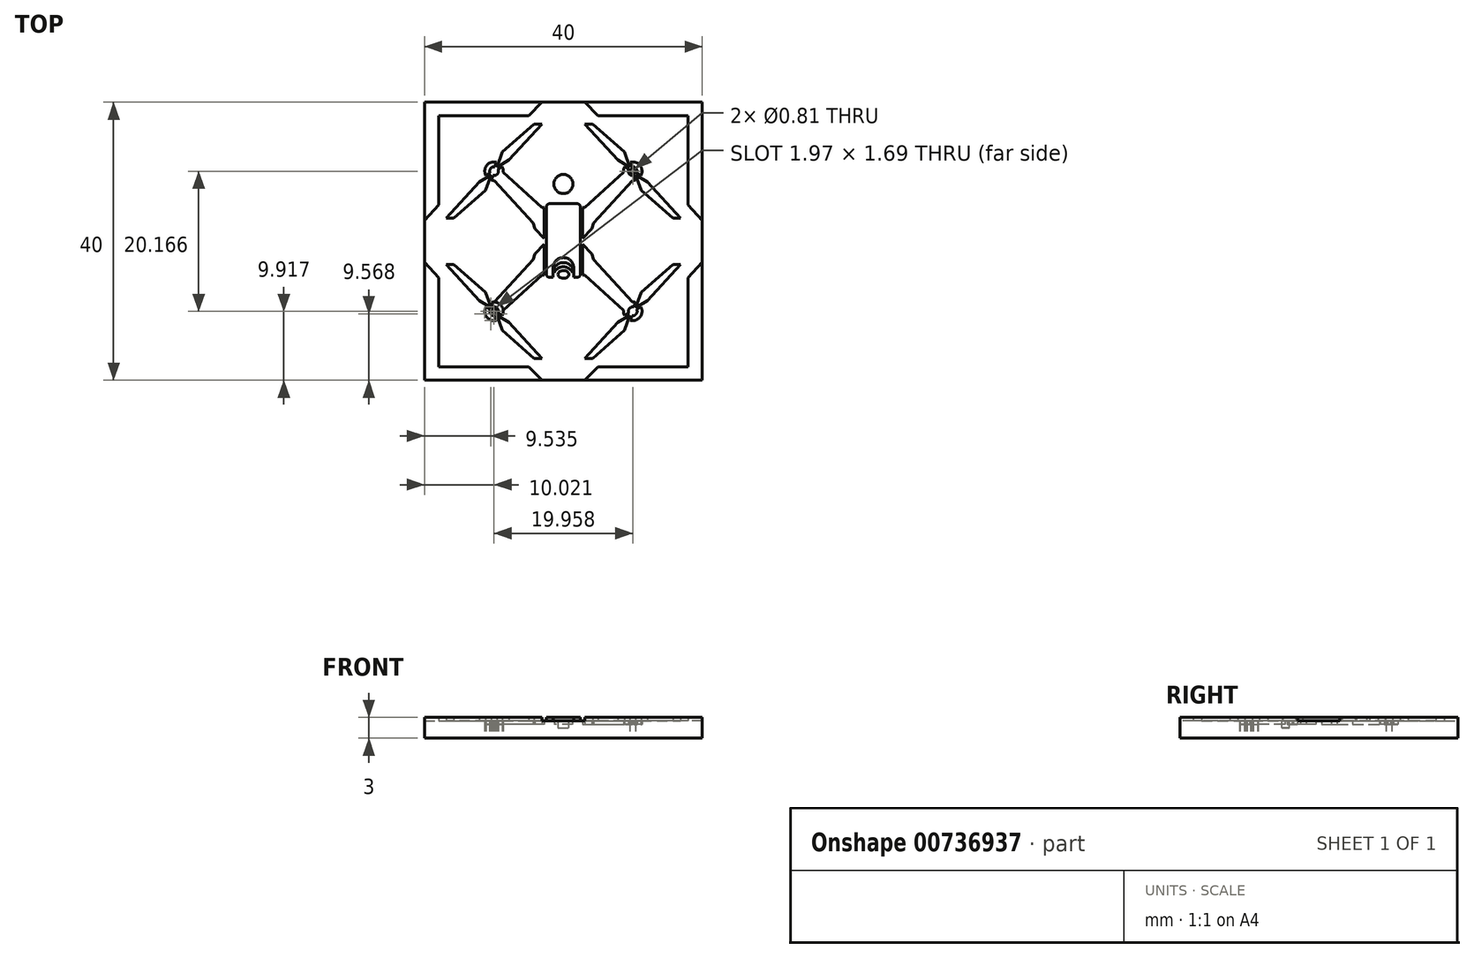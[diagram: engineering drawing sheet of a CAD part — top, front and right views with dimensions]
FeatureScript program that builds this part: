
annotation { "Feature Type Name" : "Feature", "Feature Type Description" : "" }
export const myFeature = defineFeature(function(context is Context, id is Id, definition is map)
    precondition{}
    {
        {
            var Q0;
            Q0=qCreatedBy(makeId("Top.planeOp"),FACE);
            var sketch = newSketch(context, id + "F0", { "sketchPlane" : qUnion([Q0])});
            skLineSegment(sketch, "E0.bottom", {"start": v(-20, 20) * mm, "end": v(20, 20) * mm});
            skLineSegment(sketch, "E0.top", {"start": v(-20, -20) * mm, "end": v(20, -20) * mm});
            skLineSegment(sketch, "E0.left", {"start": v(-20, 20) * mm, "end": v(-20, -20) * mm});
            skLineSegment(sketch, "E0.right", {"start": v(20, 20) * mm, "end": v(20, -20) * mm});
            skLineSegment(sketch, "E1", {"start": v(-20, 3.01) * mm, "end": v(-17.93, 5.25) * mm});
            skLineSegment(sketch, "E2", {"start": v(-17.93, 5.25) * mm, "end": v(-17.93, 18.07) * mm});
            skLineSegment(sketch, "E3", {"start": v(-17.93, 18.07) * mm, "end": v(-5, 18.07) * mm});
            skLineSegment(sketch, "E4", {"start": v(-5, 18.07) * mm, "end": v(-3.07, 20) * mm});
            skLineSegment(sketch, "E5", {"start": v(-16.86, 3.32) * mm, "end": v(-12.08, 8.54) * mm});
            skLineSegment(sketch, "E6", {"start": v(-12.08, 8.54) * mm, "end": v(-10.4, 9.57) * mm});
            skLineSegment(sketch, "E7", {"start": v(-10.4, 9.57) * mm, "end": v(-11.18, 7.35) * mm});
            skLineSegment(sketch, "E8", {"start": v(-11.18, 7.35) * mm, "end": v(-15.75, 3.32) * mm});
            skLineSegment(sketch, "E9", {"start": v(-15.75, 3.32) * mm, "end": v(-16.86, 3.32) * mm});
            skLineSegment(sketch, "E10", {"start": v(-9.53, 10.64) * mm, "end": v(-8.82, 12.83) * mm});
            skLineSegment(sketch, "E11", {"start": v(-8.82, 12.83) * mm, "end": v(-4.25, 16.86) * mm});
            skLineSegment(sketch, "E12", {"start": v(-4.25, 16.86) * mm, "end": v(-3.08, 16.86) * mm});
            skLineSegment(sketch, "E13", {"start": v(-3.08, 16.86) * mm, "end": v(-7.83, 11.68) * mm});
            skLineSegment(sketch, "E14", {"start": v(-7.83, 11.68) * mm, "end": v(-9.53, 10.64) * mm});
            skLineSegment(sketch, "E15", {"start": v(-2.75, 0.43) * mm, "end": v(-2.75, 4.84) * mm});
            skLineSegment(sketch, "E16", {"start": v(-2.75, 4.84) * mm, "end": v(-3.08, 4.84) * mm});
            skLineSegment(sketch, "E17", {"start": v(-3.08, 4.84) * mm, "end": v(-8.65, 9.93) * mm});
            skLineSegment(sketch, "E18", {"start": v(-2.75, 0.43) * mm, "end": v(-4.12, 1.8) * mm});
            skLineSegment(sketch, "E19", {"start": v(-4.12, 1.8) * mm, "end": v(-4.34, 2.63) * mm});
            skLineSegment(sketch, "E20", {"start": v(-4.34, 2.63) * mm, "end": v(-9.91, 8.74) * mm});
            skCircle(sketch, "E21", {"center": v(-9.98, 10.08) * mm, "radius": 0.4 * mm});
            skLineSegment(sketch, "E22", {"start": v(-11.15, 9.45) * mm, "end": v(-10.56, 9.84) * mm});
            skLineSegment(sketch, "E23", {"start": v(-9.86, 10.7) * mm, "end": v(-9.62, 11.37) * mm});
            skLineSegment(sketch, "E24", {"start": v(-10.14, 9.47) * mm, "end": v(-10.4, 8.82) * mm});
            skLineSegment(sketch, "E25", {"start": v(-9.4, 10.34) * mm, "end": v(-9.4, 10.34) * mm});
            skLineSegment(sketch, "E26", {"start": v(-9.4, 10.34) * mm, "end": v(-8.81, 10.73) * mm});
            skArc(sketch, "E27", {"start": v(-9.86, 10.7) * mm, "mid": v(-10.47, 10.48) * mm, "end": v(-10.56, 9.84) * mm});
            skLineSegment(sketch, "E28", {"start": v(-9.62, 11.37) * mm, "end": v(-9.62, 11.37) * mm});
            skLineSegment(sketch, "E29", {"start": v(-10.56, 9.84) * mm, "end": v(-10.56, 9.84) * mm});
            skArc(sketch, "E30", {"start": v(-10.14, 9.47) * mm, "mid": v(-9.5, 9.67) * mm, "end": v(-9.4, 10.34) * mm});
            skArc(sketch, "E31", {"start": v(-10.4, 8.82) * mm, "mid": v(-8.95, 9.23) * mm, "end": v(-8.81, 10.73) * mm});
            skArc(sketch, "E32", {"start": v(-9.62, 11.37) * mm, "mid": v(-11.02, 10.91) * mm, "end": v(-11.15, 9.45) * mm});
            skCircle(sketch, "E33.MirrorC", {"center": v(9.98, 10.08) * mm, "radius": 0.4 * mm});
            skLineSegment(sketch, "E34.MirrorCS", {"start": v(9.86, 10.7) * mm, "end": v(9.62, 11.37) * mm});
            skLineSegment(sketch, "E35.MirrorCS", {"start": v(10.14, 9.47) * mm, "end": v(10.4, 8.82) * mm});
            skLineSegment(sketch, "E36.MirrorCS", {"start": v(11.15, 9.45) * mm, "end": v(10.56, 9.84) * mm});
            skLineSegment(sketch, "E37.MirrorCS", {"start": v(15.75, 3.32) * mm, "end": v(16.86, 3.32) * mm});
            skLineSegment(sketch, "E38.MirrorCS", {"start": v(9.4, 10.34) * mm, "end": v(8.81, 10.73) * mm});
            skLineSegment(sketch, "E39.MirrorCS", {"start": v(2.75, 4.84) * mm, "end": v(3.08, 4.84) * mm});
            skLineSegment(sketch, "E40.MirrorCS", {"start": v(4.12, 1.8) * mm, "end": v(4.34, 2.63) * mm});
            skLineSegment(sketch, "E41.MirrorCS", {"start": v(4.25, 16.86) * mm, "end": v(3.08, 16.86) * mm});
            skArc(sketch, "E42.MirrorCS", {"start": v(9.86, 10.7) * mm, "mid": v(10.47, 10.48) * mm, "end": v(10.56, 9.84) * mm});
            skLineSegment(sketch, "E43.MirrorCS", {"start": v(3.08, 16.86) * mm, "end": v(7.83, 11.68) * mm});
            skArc(sketch, "E44.MirrorCS", {"start": v(9.62, 11.37) * mm, "mid": v(11.02, 10.91) * mm, "end": v(11.15, 9.45) * mm});
            skLineSegment(sketch, "E45.MirrorCS", {"start": v(2.75, 0.43) * mm, "end": v(4.12, 1.8) * mm});
            skLineSegment(sketch, "E46.MirrorCS", {"start": v(2.75, 0.43) * mm, "end": v(2.75, 4.84) * mm});
            skLineSegment(sketch, "E47.MirrorCS", {"start": v(17.93, 5.25) * mm, "end": v(17.93, 18.07) * mm});
            skLineSegment(sketch, "E48.MirrorCS", {"start": v(8.82, 12.83) * mm, "end": v(4.25, 16.86) * mm});
            skLineSegment(sketch, "E49.MirrorCS", {"start": v(4.34, 2.63) * mm, "end": v(9.91, 8.74) * mm});
            skLineSegment(sketch, "E50.MirrorCS", {"start": v(17.93, 18.07) * mm, "end": v(5, 18.07) * mm});
            skArc(sketch, "E51.MirrorCS", {"start": v(10.14, 9.47) * mm, "mid": v(9.5, 9.67) * mm, "end": v(9.4, 10.34) * mm});
            skLineSegment(sketch, "E52.MirrorCS", {"start": v(3.08, 4.84) * mm, "end": v(8.65, 9.93) * mm});
            skLineSegment(sketch, "E53.MirrorCS", {"start": v(7.83, 11.68) * mm, "end": v(9.53, 10.64) * mm});
            skLineSegment(sketch, "E54.MirrorCS", {"start": v(9.53, 10.64) * mm, "end": v(8.82, 12.83) * mm});
            skLineSegment(sketch, "E55.MirrorCS", {"start": v(16.86, 3.32) * mm, "end": v(12.08, 8.54) * mm});
            skLineSegment(sketch, "E56.MirrorCS", {"start": v(12.08, 8.54) * mm, "end": v(10.4, 9.57) * mm});
            skArc(sketch, "E57.MirrorCS", {"start": v(10.4, 8.82) * mm, "mid": v(8.95, 9.23) * mm, "end": v(8.81, 10.73) * mm});
            skLineSegment(sketch, "E58.MirrorCS", {"start": v(5, 18.07) * mm, "end": v(3.07, 20) * mm});
            skLineSegment(sketch, "E59.MirrorCS", {"start": v(20, 3.01) * mm, "end": v(17.93, 5.25) * mm});
            skLineSegment(sketch, "E60.MirrorCS", {"start": v(11.18, 7.35) * mm, "end": v(15.75, 3.32) * mm});
            skLineSegment(sketch, "E61.MirrorCS", {"start": v(10.4, 9.57) * mm, "end": v(11.18, 7.35) * mm});
            skArc(sketch, "E62.MirrorCS", {"start": v(-10.14, -9.47) * mm, "mid": v(-9.5, -9.67) * mm, "end": v(-9.4, -10.34) * mm});
            skCircle(sketch, "E63.MirrorC", {"center": v(-9.98, -10.08) * mm, "radius": 0.4 * mm});
            skArc(sketch, "E64.MirrorCS", {"start": v(-9.86, -10.7) * mm, "mid": v(-10.47, -10.48) * mm, "end": v(-10.56, -9.84) * mm});
            skLineSegment(sketch, "E65.MirrorCS", {"start": v(-9.86, -10.7) * mm, "end": v(-9.62, -11.37) * mm});
            skLineSegment(sketch, "E66.MirrorCS", {"start": v(-11.15, -9.45) * mm, "end": v(-10.56, -9.84) * mm});
            skLineSegment(sketch, "E67.MirrorCS", {"start": v(-9.4, -10.34) * mm, "end": v(-8.81, -10.73) * mm});
            skArc(sketch, "E68.MirrorCS", {"start": v(9.86, -10.7) * mm, "mid": v(10.47, -10.48) * mm, "end": v(10.56, -9.84) * mm});
            skLineSegment(sketch, "E69.MirrorCS", {"start": v(11.15, -9.45) * mm, "end": v(10.56, -9.84) * mm});
            skLineSegment(sketch, "E70.MirrorCS", {"start": v(9.86, -10.7) * mm, "end": v(9.62, -11.37) * mm});
            skCircle(sketch, "E71.MirrorC", {"center": v(9.98, -10.08) * mm, "radius": 0.4 * mm});
            skLineSegment(sketch, "E72.MirrorCS", {"start": v(9.4, -10.34) * mm, "end": v(8.81, -10.73) * mm});
            skArc(sketch, "E73.MirrorCS", {"start": v(10.14, -9.47) * mm, "mid": v(9.5, -9.67) * mm, "end": v(9.4, -10.34) * mm});
            skLineSegment(sketch, "E74.MirrorCS", {"start": v(-10.14, -9.47) * mm, "end": v(-10.4, -8.82) * mm});
            skArc(sketch, "E75.MirrorCS", {"start": v(-9.62, -11.37) * mm, "mid": v(-11.02, -10.91) * mm, "end": v(-11.15, -9.45) * mm});
            skArc(sketch, "E76.MirrorCS", {"start": v(-10.4, -8.82) * mm, "mid": v(-8.95, -9.23) * mm, "end": v(-8.81, -10.73) * mm});
            skLineSegment(sketch, "E77.MirrorCS", {"start": v(10.14, -9.47) * mm, "end": v(10.4, -8.82) * mm});
            skLineSegment(sketch, "E78.MirrorCS", {"start": v(-7.83, -11.68) * mm, "end": v(-9.53, -10.64) * mm});
            skArc(sketch, "E79.MirrorCS", {"start": v(10.4, -8.82) * mm, "mid": v(8.95, -9.23) * mm, "end": v(8.81, -10.73) * mm});
            skArc(sketch, "E80.MirrorCS", {"start": v(9.62, -11.37) * mm, "mid": v(11.02, -10.91) * mm, "end": v(11.15, -9.45) * mm});
            skLineSegment(sketch, "E81.MirrorCS", {"start": v(9.53, -10.64) * mm, "end": v(8.82, -12.83) * mm});
            skLineSegment(sketch, "E82.MirrorCS", {"start": v(4.12, -1.8) * mm, "end": v(4.34, -2.63) * mm});
            skLineSegment(sketch, "E83.MirrorCS", {"start": v(-2.75, -0.43) * mm, "end": v(-4.12, -1.8) * mm});
            skLineSegment(sketch, "E84.MirrorCS", {"start": v(15.75, -3.32) * mm, "end": v(16.86, -3.32) * mm});
            skLineSegment(sketch, "E85.MirrorCS", {"start": v(2.75, -4.84) * mm, "end": v(3.08, -4.84) * mm});
            skLineSegment(sketch, "E86.MirrorCS", {"start": v(7.83, -11.68) * mm, "end": v(9.53, -10.64) * mm});
            skLineSegment(sketch, "E87.MirrorCS", {"start": v(2.75, -0.43) * mm, "end": v(4.12, -1.8) * mm});
            skLineSegment(sketch, "E88.MirrorCS", {"start": v(10.4, -9.57) * mm, "end": v(11.18, -7.35) * mm});
            skLineSegment(sketch, "E89.MirrorCS", {"start": v(-9.53, -10.64) * mm, "end": v(-8.82, -12.83) * mm});
            skLineSegment(sketch, "E90.MirrorCS", {"start": v(-4.25, -16.86) * mm, "end": v(-3.08, -16.86) * mm});
            skLineSegment(sketch, "E91.MirrorCS", {"start": v(-4.12, -1.8) * mm, "end": v(-4.34, -2.63) * mm});
            skLineSegment(sketch, "E92.MirrorCS", {"start": v(-12.08, -8.54) * mm, "end": v(-10.4, -9.57) * mm});
            skLineSegment(sketch, "E93.MirrorCS", {"start": v(-10.4, -9.57) * mm, "end": v(-11.18, -7.35) * mm});
            skLineSegment(sketch, "E94.MirrorCS", {"start": v(12.08, -8.54) * mm, "end": v(10.4, -9.57) * mm});
            skLineSegment(sketch, "E95.MirrorCS", {"start": v(4.25, -16.86) * mm, "end": v(3.08, -16.86) * mm});
            skLineSegment(sketch, "E96.MirrorCS", {"start": v(-2.75, -4.84) * mm, "end": v(-3.08, -4.84) * mm});
            skLineSegment(sketch, "E97.MirrorCS", {"start": v(-15.75, -3.32) * mm, "end": v(-16.86, -3.32) * mm});
            skLineSegment(sketch, "E98.MirrorCS", {"start": v(20, -3.01) * mm, "end": v(17.93, -5.25) * mm});
            skLineSegment(sketch, "E99.MirrorCS", {"start": v(5, -18.07) * mm, "end": v(3.07, -20) * mm});
            skLineSegment(sketch, "E100.MirrorCS", {"start": v(-5, -18.07) * mm, "end": v(-3.07, -20) * mm});
            skLineSegment(sketch, "E101.MirrorCS", {"start": v(-2.75, -0.43) * mm, "end": v(-2.75, -4.84) * mm});
            skLineSegment(sketch, "E102.MirrorCS", {"start": v(2.75, -0.43) * mm, "end": v(2.75, -4.84) * mm});
            skLineSegment(sketch, "E103.MirrorCS", {"start": v(-8.82, -12.83) * mm, "end": v(-4.25, -16.86) * mm});
            skLineSegment(sketch, "E104.MirrorCS", {"start": v(-3.08, -16.86) * mm, "end": v(-7.83, -11.68) * mm});
            skLineSegment(sketch, "E105.MirrorCS", {"start": v(-4.34, -2.63) * mm, "end": v(-9.91, -8.74) * mm});
            skLineSegment(sketch, "E106.MirrorCS", {"start": v(16.86, -3.32) * mm, "end": v(12.08, -8.54) * mm});
            skLineSegment(sketch, "E107.MirrorCS", {"start": v(3.08, -16.86) * mm, "end": v(7.83, -11.68) * mm});
            skLineSegment(sketch, "E108.MirrorCS", {"start": v(-3.08, -4.84) * mm, "end": v(-8.65, -9.93) * mm});
            skLineSegment(sketch, "E109.MirrorCS", {"start": v(3.08, -4.84) * mm, "end": v(8.65, -9.93) * mm});
            skLineSegment(sketch, "E110.MirrorCS", {"start": v(17.93, -5.25) * mm, "end": v(17.93, -18.07) * mm});
            skLineSegment(sketch, "E111.MirrorCS", {"start": v(-11.18, -7.35) * mm, "end": v(-15.75, -3.32) * mm});
            skLineSegment(sketch, "E112.MirrorCS", {"start": v(4.34, -2.63) * mm, "end": v(9.91, -8.74) * mm});
            skLineSegment(sketch, "E113.MirrorCS", {"start": v(8.82, -12.83) * mm, "end": v(4.25, -16.86) * mm});
            skLineSegment(sketch, "E114.MirrorCS", {"start": v(-16.86, -3.32) * mm, "end": v(-12.08, -8.54) * mm});
            skLineSegment(sketch, "E115.MirrorCS", {"start": v(11.18, -7.35) * mm, "end": v(15.75, -3.32) * mm});
            skLineSegment(sketch, "E116.MirrorCS", {"start": v(-17.93, -18.07) * mm, "end": v(-5, -18.07) * mm});
            skLineSegment(sketch, "E117.MirrorCS", {"start": v(17.93, -18.07) * mm, "end": v(5, -18.07) * mm});
            skLineSegment(sketch, "E118.MirrorCS", {"start": v(-20, -3.01) * mm, "end": v(-17.93, -5.25) * mm});
            skLineSegment(sketch, "E119.MirrorCS", {"start": v(-17.93, -5.25) * mm, "end": v(-17.93, -18.07) * mm});
            skCircle(sketch, "E120", {"center": v(0, 8.24) * mm, "radius": 1.38 * mm});
            skLineSegment(sketch, "E121.bottom", {"start": v(0, 6.7) * mm, "end": v(-0.2, 6.7) * mm});
            skLineSegment(sketch, "E121.top", {"start": v(0, 5.7) * mm, "end": v(-0.2, 5.7) * mm});
            skLineSegment(sketch, "E121.left", {"start": v(0, 6.7) * mm, "end": v(0, 5.7) * mm});
            skLineSegment(sketch, "E121.right", {"start": v(-0.2, 6.7) * mm, "end": v(-0.2, 5.7) * mm});
            skLineSegment(sketch, "E122", {"start": v(0, 5.4) * mm, "end": v(-1.96, 5.4) * mm});
            skLineSegment(sketch, "E123", {"start": v(-2.46, 4.9) * mm, "end": v(-2.46, -4.7) * mm});
            skLineSegment(sketch, "E124", {"start": v(-1.96, -5.2) * mm, "end": v(-1.49, -5.2) * mm});
            skLineSegment(sketch, "E125", {"start": v(-1.49, -5.2) * mm, "end": v(-1.49, -3.84) * mm});
            skLineSegment(sketch, "E126", {"start": v(0, -2.35) * mm, "end": v(0, -2.35) * mm});
            skLineSegment(sketch, "E127", {"start": v(0, -2.35) * mm, "end": v(0, 5.4) * mm});
            skPoint(sketch, "E128.visualSharp", {"position": v(-2.46, 5.4) * mm});
            skArc(sketch, "E128.filletArc", {"start": v(-1.96, 5.4) * mm, "mid": v(-2.3, 5.26) * mm, "end": v(-2.46, 4.9) * mm});
            skPoint(sketch, "E129.visualSharp", {"position": v(-2.46, -5.2) * mm});
            skArc(sketch, "E129.filletArc", {"start": v(-2.46, -4.7) * mm, "mid": v(-2.3, -5.06) * mm, "end": v(-1.96, -5.2) * mm});
            skPoint(sketch, "E130.visualSharp", {"position": v(-1.49, -2.35) * mm});
            skArc(sketch, "E130.filletArc", {"start": v(0, -2.35) * mm, "mid": v(-1.05, -2.79) * mm, "end": v(-1.49, -3.84) * mm});
            skArc(sketch, "E131.MirrorCS", {"start": v(0, -2.35) * mm, "mid": v(1.05, -2.79) * mm, "end": v(1.49, -3.84) * mm});
            skLineSegment(sketch, "E132.MirrorCS", {"start": v(1.49, -5.2) * mm, "end": v(1.49, -3.84) * mm});
            skLineSegment(sketch, "E133.MirrorCS", {"start": v(1.96, -5.2) * mm, "end": v(1.49, -5.2) * mm});
            skArc(sketch, "E134.MirrorCS", {"start": v(2.46, -4.7) * mm, "mid": v(2.3, -5.06) * mm, "end": v(1.96, -5.2) * mm});
            skLineSegment(sketch, "E135.MirrorCS", {"start": v(2.46, 4.9) * mm, "end": v(2.46, -4.7) * mm});
            skArc(sketch, "E136.MirrorCS", {"start": v(1.96, 5.4) * mm, "mid": v(2.3, 5.26) * mm, "end": v(2.46, 4.9) * mm});
            skLineSegment(sketch, "E137.MirrorCS", {"start": v(0, 5.4) * mm, "end": v(1.96, 5.4) * mm});
            skLineSegment(sketch, "E138.MirrorCS", {"start": v(0, 5.7) * mm, "end": v(0.2, 5.7) * mm});
            skLineSegment(sketch, "E139.MirrorCS", {"start": v(0.2, 6.7) * mm, "end": v(0.2, 5.7) * mm});
            skLineSegment(sketch, "E140.MirrorCS", {"start": v(0, 6.7) * mm, "end": v(0.2, 6.7) * mm});
            skEllipse(sketch, "E141", {"center": v(0, -4.77) * mm, "majorRadius": 0.78 * mm, "minorRadius": 0.55 * mm, "majorAxis": v(-1, 0)});
            skEllipse(sketch, "E142", {"center": v(0, -4.77) * mm, "majorRadius": 1.19 * mm, "minorRadius": 0.84 * mm, "majorAxis": v(-1, 0)});
            skLineSegment(sketch, "E143", {"start": v(-1.33, -4.52) * mm, "end": v(-1.33, -3.84) * mm});
            skPoint(sketch, "E143.startSnap0", {"position": v(-1.49, -4.52) * mm});
            skLineSegment(sketch, "E144", {"start": v(1.32, -3.84) * mm, "end": v(1.32, -4.52) * mm});
            skLineSegment(sketch, "E145", {"start": v(9.91, -8.74) * mm, "end": v(9.92, -8.75) * mm});
            skLineSegment(sketch, "E146", {"start": v(9.91, 8.74) * mm, "end": v(9.92, 8.75) * mm});
            skLineSegment(sketch, "E147", {"start": v(-9.91, 8.74) * mm, "end": v(-9.92, 8.75) * mm});
            skLineSegment(sketch, "E148", {"start": v(-9.91, -8.74) * mm, "end": v(-9.92, -8.75) * mm});
            skArc(sketch, "E149", {"start": v(1.32, -3.84) * mm, "mid": v(0, -3.06) * mm, "end": v(-1.33, -3.84) * mm});
            skArc(sketch, "E150", {"start": v(1.32, -4.52) * mm, "mid": v(0, -3.67) * mm, "end": v(-1.33, -4.52) * mm});
            skSolve(sketch);
        }
        {
            var Q0;
            {var subQ19=sQuery(id+"F0.wireOp",EDGE,"E1");Q0=makeQuery(id+"F0.imprint","IMPRINT",FACE,{"disambiguationData":[TD([[makeQuery(id+"F0.imprint","IMPRINT",EDGE,{"derivedFrom":subQ19}),-1.0]])]});}
            var Q1;
            Q1=makeQuery(id+"F0.imprint","IMPRINT",FACE,{"disambiguationData":[TD([[makeQuery(id+"F0.imprint","IMPRINT",EDGE,{"derivedFrom":sQuery(id+"F0.wireOp",EDGE,"E84.MirrorCS")}),-1.0]])]});
            var Q2;
            Q2=makeQuery(id+"F0.imprint","IMPRINT",FACE,{"disambiguationData":[TD([[makeQuery(id+"F0.imprint","IMPRINT",EDGE,{"derivedFrom":sQuery(id+"F0.wireOp",EDGE,"E41.MirrorCS")}),1.0]])]});
            var Q3;
            {var subQ0=sQuery(id+"F0.wireOp",EDGE,"E1");Q3=makeQuery(id+"F0.imprint","IMPRINT",FACE,{"disambiguationData":[TD([[makeQuery(id+"F0.imprint","IMPRINT",EDGE,{"derivedFrom":subQ0}),1.0]])]});}
            var Q4;
            Q4=makeQuery(id+"F0.imprint","IMPRINT",FACE,{"disambiguationData":[TD([[makeQuery(id+"F0.imprint","IMPRINT",EDGE,{"derivedFrom":sQuery(id+"F0.wireOp",EDGE,"E47.MirrorCS")}),-1.0]])]});
            var Q5;
            Q5=makeQuery(id+"F0.imprint","IMPRINT",FACE,{"disambiguationData":[TD([[makeQuery(id+"F0.imprint","IMPRINT",EDGE,{"derivedFrom":sQuery(id+"F0.wireOp",EDGE,"E81.MirrorCS")}),-1.0]])]});
            var Q6;
            Q6=makeQuery(id+"F0.imprint","IMPRINT",FACE,{"disambiguationData":[TD([[makeQuery(id+"F0.imprint","IMPRINT",EDGE,{"derivedFrom":sQuery(id+"F0.wireOp",EDGE,"E5")}),-1.0]])]});
            var Q7;
            Q7=makeQuery(id+"F0.imprint","IMPRINT",FACE,{"disambiguationData":[TD([[makeQuery(id+"F0.imprint","IMPRINT",EDGE,{"derivedFrom":sQuery(id+"F0.wireOp",EDGE,"E78.MirrorCS")}),1.0]])]});
            var Q8;
            {var subQ4=sQuery(id+"F0.wireOp",EDGE,"E100.MirrorCS");Q8=makeQuery(id+"F0.imprint","IMPRINT",FACE,{"disambiguationData":[TD([[makeQuery(id+"F0.imprint","IMPRINT",EDGE,{"derivedFrom":subQ4}),-1.0]])]});}
            var Q9;
            Q9=makeQuery(id+"F0.imprint","IMPRINT",FACE,{"disambiguationData":[TD([[makeQuery(id+"F0.imprint","IMPRINT",EDGE,{"derivedFrom":sQuery(id+"F0.wireOp",EDGE,"E10")}),-1.0]])]});
            var Q10;
            {var subQ3=sQuery(id+"F0.wireOp",EDGE,"E98.MirrorCS");Q10=makeQuery(id+"F0.imprint","IMPRINT",FACE,{"disambiguationData":[TD([[makeQuery(id+"F0.imprint","IMPRINT",EDGE,{"derivedFrom":subQ3}),1.0]])]});}
            var Q11;
            Q11=makeQuery(id+"F0.imprint","IMPRINT",FACE,{"disambiguationData":[TD([[makeQuery(id+"F0.imprint","IMPRINT",EDGE,{"derivedFrom":sQuery(id+"F0.wireOp",EDGE,"E37.MirrorCS")}),1.0]])]});
            var Q12;
            Q12=makeQuery(id+"F0.imprint","IMPRINT",FACE,{"disambiguationData":[TD([[makeQuery(id+"F0.imprint","IMPRINT",EDGE,{"derivedFrom":sQuery(id+"F0.wireOp",EDGE,"E92.MirrorCS")}),1.0]])]});
            var Q13;
            Q13=makeQuery(id+"F0.imprint","IMPRINT",FACE,{"disambiguationData":[TD([[makeQuery(id+"F0.imprint","IMPRINT",EDGE,{"derivedFrom":sQuery(id+"F0.wireOp",EDGE,"E122")}),1.0]])]});
            var Q14;
            Q14=makeQuery(id+"F0.imprint","IMPRINT",FACE,{"disambiguationData":[TD([[makeQuery(id+"F0.imprint","IMPRINT",EDGE,{"derivedFrom":sQuery(id+"F0.wireOp",EDGE,"E64.MirrorCS")}),1.0]])]});
            var Q15;
            Q15=makeQuery(id+"F0.imprint","IMPRINT",FACE,{"disambiguationData":[TD([[makeQuery(id+"F0.imprint","IMPRINT",EDGE,{"derivedFrom":sQuery(id+"F0.wireOp",EDGE,"E120")}),1.0]])]});
            var Q16;
            Q16=makeQuery(id+"F0.imprint","IMPRINT",FACE,{"disambiguationData":[TD([[makeQuery(id+"F0.imprint","IMPRINT",EDGE,{"derivedFrom":sQuery(id+"F0.wireOp",EDGE,"E22")}),1.0]])]});
            var Q17;
            Q17=makeQuery(id+"F0.imprint","IMPRINT",FACE,{"disambiguationData":[TD([[makeQuery(id+"F0.imprint","IMPRINT",EDGE,{"derivedFrom":sQuery(id+"F0.wireOp",EDGE,"E34.MirrorCS")}),-1.0]])]});
            var Q18;
            {var subQ2=sQuery(id+"F0.wireOp",EDGE,"E24");Q18=makeQuery(id+"F0.imprint","IMPRINT",FACE,{"disambiguationData":[TD([[makeQuery(id+"F0.imprint","IMPRINT",EDGE,{"derivedFrom":subQ2}),1.0]])]});}
            var Q19;
            {var subQ1=sQuery(id+"F0.wireOp",EDGE,"E35.MirrorCS");Q19=makeQuery(id+"F0.imprint","IMPRINT",FACE,{"disambiguationData":[TD([[makeQuery(id+"F0.imprint","IMPRINT",EDGE,{"derivedFrom":subQ1}),-1.0]])]});}
            var Q20;
            Q20=makeQuery(id+"F0.imprint","IMPRINT",FACE,{"disambiguationData":[TD([[makeQuery(id+"F0.imprint","IMPRINT",EDGE,{"derivedFrom":sQuery(id+"F0.wireOp",EDGE,"E68.MirrorCS")}),-1.0]])]});
            var Q21;
            Q21=makeQuery(id+"F0.imprint","IMPRINT",FACE,{"disambiguationData":[TD([[makeQuery(id+"F0.imprint","IMPRINT",EDGE,{"derivedFrom":sQuery(id+"F0.wireOp",EDGE,"E62.MirrorCS")}),1.0]])]});
            var Q22;
            Q22=makeQuery(id+"F0.imprint","IMPRINT",FACE,{"disambiguationData":[TD([[makeQuery(id+"F0.imprint","IMPRINT",EDGE,{"derivedFrom":sQuery(id+"F0.wireOp",EDGE,"E141")}),-1.0]])]});
            var Q23;
            Q23=makeQuery(id+"F0.imprint","IMPRINT",FACE,{"disambiguationData":[TD([[makeQuery(id+"F0.imprint","IMPRINT",EDGE,{"derivedFrom":sQuery(id+"F0.wireOp",EDGE,"E141")}),1.0]])]});
            var Q24;
            {var subQ3=sQuery(id+"F0.wireOp",EDGE,"E72.MirrorCS");Q24=makeQuery(id+"F0.imprint","IMPRINT",FACE,{"disambiguationData":[TD([[makeQuery(id+"F0.imprint","IMPRINT",EDGE,{"derivedFrom":subQ3}),-1.0]])]});}
            var Q25;
            Q25=makeQuery(id+"F0.imprint","IMPRINT",FACE,{"disambiguationData":[TD([[makeQuery(id+"F0.imprint","IMPRINT",EDGE,{"derivedFrom":sQuery(id+"F0.wireOp",EDGE,"E63.MirrorC")}),-1.0]])]});
            var Q26;
            Q26=makeQuery(id+"F0.imprint","IMPRINT",FACE,{"disambiguationData":[TD([[makeQuery(id+"F0.imprint","IMPRINT",EDGE,{"derivedFrom":sQuery(id+"F0.wireOp",EDGE,"E71.MirrorC")}),1.0]])]});
            var Q27;
            Q27=makeQuery(id+"F0.imprint","IMPRINT",FACE,{"disambiguationData":[TD([[makeQuery(id+"F0.imprint","IMPRINT",EDGE,{"derivedFrom":sQuery(id+"F0.wireOp",EDGE,"E33.MirrorC")}),-1.0]])]});
            var Q28;
            Q28=makeQuery(id+"F0.imprint","IMPRINT",FACE,{"disambiguationData":[TD([[makeQuery(id+"F0.imprint","IMPRINT",EDGE,{"derivedFrom":sQuery(id+"F0.wireOp",EDGE,"E21")}),1.0]])]});
            var Q29;
            Q29=makeQuery(id+"F0.imprint","IMPRINT",FACE,{"disambiguationData":[TD([[makeQuery(id+"F0.imprint","IMPRINT",EDGE,{"derivedFrom":sQuery(id+"F0.wireOp",EDGE,"E121.left")}),1.0]])]});
            var Q30;
            Q30=makeQuery(id+"F0.imprint","IMPRINT",FACE,{"disambiguationData":[TD([[makeQuery(id+"F0.imprint","IMPRINT",EDGE,{"derivedFrom":sQuery(id+"F0.wireOp",EDGE,"E121.bottom")}),1.0]])]});
            extrude(context, id + "F1", {"entities" : qUnion([Q0, Q1, Q2, Q3, Q4, Q5, Q6, Q7, Q8, Q9, Q10, Q11, Q12, Q13, Q14, Q15, Q16, Q17, Q18, Q19, Q20, Q21, Q22, Q23, Q24, Q25, Q26, Q27, Q28, Q29, Q30]), "depth" : 1.5 * mm, "offsetDistance" : 25 * mm});
        }
        {
            var Q0;
            {var subQ0=sQuery(id+"F0.wireOp",EDGE,"E1");Q0=makeQuery(id+"F0.imprint","IMPRINT",FACE,{"disambiguationData":[TD([[makeQuery(id+"F0.imprint","IMPRINT",EDGE,{"derivedFrom":subQ0}),1.0]])]});}
            var Q1;
            {var subQ4=sQuery(id+"F0.wireOp",EDGE,"E100.MirrorCS");Q1=makeQuery(id+"F0.imprint","IMPRINT",FACE,{"disambiguationData":[TD([[makeQuery(id+"F0.imprint","IMPRINT",EDGE,{"derivedFrom":subQ4}),-1.0]])]});}
            var Q2;
            {var subQ3=sQuery(id+"F0.wireOp",EDGE,"E98.MirrorCS");Q2=makeQuery(id+"F0.imprint","IMPRINT",FACE,{"disambiguationData":[TD([[makeQuery(id+"F0.imprint","IMPRINT",EDGE,{"derivedFrom":subQ3}),1.0]])]});}
            var Q3;
            Q3=makeQuery(id+"F0.imprint","IMPRINT",FACE,{"disambiguationData":[TD([[makeQuery(id+"F0.imprint","IMPRINT",EDGE,{"derivedFrom":sQuery(id+"F0.wireOp",EDGE,"E47.MirrorCS")}),-1.0]])]});
            var Q4;
            Q4=makeQuery(id+"F0.imprint","IMPRINT",FACE,{"disambiguationData":[TD([[makeQuery(id+"F0.imprint","IMPRINT",EDGE,{"derivedFrom":sQuery(id+"F0.wireOp",EDGE,"E78.MirrorCS")}),1.0]])]});
            var Q5;
            Q5=makeQuery(id+"F0.imprint","IMPRINT",FACE,{"disambiguationData":[TD([[makeQuery(id+"F0.imprint","IMPRINT",EDGE,{"derivedFrom":sQuery(id+"F0.wireOp",EDGE,"E92.MirrorCS")}),1.0]])]});
            var Q6;
            Q6=makeQuery(id+"F0.imprint","IMPRINT",FACE,{"disambiguationData":[TD([[makeQuery(id+"F0.imprint","IMPRINT",EDGE,{"derivedFrom":sQuery(id+"F0.wireOp",EDGE,"E81.MirrorCS")}),-1.0]])]});
            var Q7;
            Q7=makeQuery(id+"F0.imprint","IMPRINT",FACE,{"disambiguationData":[TD([[makeQuery(id+"F0.imprint","IMPRINT",EDGE,{"derivedFrom":sQuery(id+"F0.wireOp",EDGE,"E84.MirrorCS")}),-1.0]])]});
            var Q8;
            Q8=makeQuery(id+"F0.imprint","IMPRINT",FACE,{"disambiguationData":[TD([[makeQuery(id+"F0.imprint","IMPRINT",EDGE,{"derivedFrom":sQuery(id+"F0.wireOp",EDGE,"E37.MirrorCS")}),1.0]])]});
            var Q9;
            Q9=makeQuery(id+"F0.imprint","IMPRINT",FACE,{"disambiguationData":[TD([[makeQuery(id+"F0.imprint","IMPRINT",EDGE,{"derivedFrom":sQuery(id+"F0.wireOp",EDGE,"E41.MirrorCS")}),1.0]])]});
            var Q10;
            Q10=makeQuery(id+"F0.imprint","IMPRINT",FACE,{"disambiguationData":[TD([[makeQuery(id+"F0.imprint","IMPRINT",EDGE,{"derivedFrom":sQuery(id+"F0.wireOp",EDGE,"E10")}),-1.0]])]});
            var Q11;
            Q11=makeQuery(id+"F0.imprint","IMPRINT",FACE,{"disambiguationData":[TD([[makeQuery(id+"F0.imprint","IMPRINT",EDGE,{"derivedFrom":sQuery(id+"F0.wireOp",EDGE,"E5")}),-1.0]])]});
            var Q12;
            Q12=makeQuery(id+"F0.imprint","IMPRINT",FACE,{"disambiguationData":[TD([[makeQuery(id+"F0.imprint","IMPRINT",EDGE,{"derivedFrom":sQuery(id+"F0.wireOp",EDGE,"E122")}),1.0]])]});
            var Q13;
            Q13=makeQuery(id+"F0.imprint","IMPRINT",FACE,{"disambiguationData":[TD([[makeQuery(id+"F0.imprint","IMPRINT",EDGE,{"derivedFrom":sQuery(id+"F0.wireOp",EDGE,"E127")}),-1.0]])]});
            var Q14;
            Q14=makeQuery(id+"F0.imprint","IMPRINT",FACE,{"disambiguationData":[TD([[makeQuery(id+"F0.imprint","IMPRINT",EDGE,{"derivedFrom":sQuery(id+"F0.wireOp",EDGE,"E120")}),1.0]])]});
            extrude(context, id + "F2", {"entities" : qUnion([Q0, Q1, Q2, Q3, Q4, Q5, Q6, Q7, Q8, Q9, Q10, Q11, Q12, Q13, Q14]), "operationType" : NewBodyOperationType.ADD, "depth" : 3 * mm, "offsetDistance" : 25 * mm});
        }
        {
            var Q0;
            Q0=makeQuery(id+"F0.imprint","IMPRINT",FACE,{"disambiguationData":[TD([[makeQuery(id+"F0.imprint","IMPRINT",EDGE,{"derivedFrom":sQuery(id+"F0.wireOp",EDGE,"E121.bottom")}),1.0]])]});
            var Q1;
            Q1=makeQuery(id+"F0.imprint","IMPRINT",FACE,{"disambiguationData":[TD([[makeQuery(id+"F0.imprint","IMPRINT",EDGE,{"derivedFrom":sQuery(id+"F0.wireOp",EDGE,"E121.left")}),1.0]])]});
            var Q2;
            Q2=makeQuery(id+"F0.imprint","IMPRINT",FACE,{"disambiguationData":[TD([[makeQuery(id+"F0.imprint","IMPRINT",EDGE,{"derivedFrom":sQuery(id+"F0.wireOp",EDGE,"E141")}),-1.0]])]});
            var Q3;
            Q3=makeQuery(id+"F0.imprint","IMPRINT",FACE,{"disambiguationData":[TD([[makeQuery(id+"F0.imprint","IMPRINT",EDGE,{"derivedFrom":sQuery(id+"F0.wireOp",EDGE,"E21")}),1.0]])]});
            var Q4;
            Q4=makeQuery(id+"F0.imprint","IMPRINT",FACE,{"disambiguationData":[TD([[makeQuery(id+"F0.imprint","IMPRINT",EDGE,{"derivedFrom":sQuery(id+"F0.wireOp",EDGE,"E33.MirrorC")}),-1.0]])]});
            var Q5;
            Q5=makeQuery(id+"F0.imprint","IMPRINT",FACE,{"disambiguationData":[TD([[makeQuery(id+"F0.imprint","IMPRINT",EDGE,{"derivedFrom":sQuery(id+"F0.wireOp",EDGE,"E71.MirrorC")}),1.0]])]});
            var Q6;
            Q6=makeQuery(id+"F0.imprint","IMPRINT",FACE,{"disambiguationData":[TD([[makeQuery(id+"F0.imprint","IMPRINT",EDGE,{"derivedFrom":sQuery(id+"F0.wireOp",EDGE,"E63.MirrorC")}),-1.0]])]});
            extrude(context, id + "F3", {"entities" : qUnion([Q0, Q1, Q2, Q3, Q4, Q5, Q6]), "operationType" : NewBodyOperationType.ADD, "depth" : 2.5 * mm, "offsetDistance" : 25 * mm});
        }
        {
            var Q0;
            Q0=makeQuery(id+"F0.imprint","IMPRINT",FACE,{"disambiguationData":[TD([[makeQuery(id+"F0.imprint","IMPRINT",EDGE,{"derivedFrom":sQuery(id+"F0.wireOp",EDGE,"E64.MirrorCS")}),1.0]])]});
            var Q1;
            Q1=makeQuery(id+"F0.imprint","IMPRINT",FACE,{"disambiguationData":[TD([[makeQuery(id+"F0.imprint","IMPRINT",EDGE,{"derivedFrom":sQuery(id+"F0.wireOp",EDGE,"E62.MirrorCS")}),1.0]])]});
            var Q2;
            Q2=makeQuery(id+"F0.imprint","IMPRINT",FACE,{"disambiguationData":[TD([[makeQuery(id+"F0.imprint","IMPRINT",EDGE,{"derivedFrom":sQuery(id+"F0.wireOp",EDGE,"E83.MirrorCS")}),1.0]])]});
            var Q3;
            Q3=makeQuery(id+"F0.imprint","IMPRINT",FACE,{"disambiguationData":[TD([[makeQuery(id+"F0.imprint","IMPRINT",EDGE,{"derivedFrom":sQuery(id+"F0.wireOp",EDGE,"E15")}),1.0]])]});
            var Q4;
            {var subQ1=sQuery(id+"F0.wireOp",EDGE,"E24");Q4=makeQuery(id+"F0.imprint","IMPRINT",FACE,{"disambiguationData":[TD([[makeQuery(id+"F0.imprint","IMPRINT",EDGE,{"derivedFrom":subQ1}),1.0]])]});}
            var Q5;
            Q5=makeQuery(id+"F0.imprint","IMPRINT",FACE,{"disambiguationData":[TD([[makeQuery(id+"F0.imprint","IMPRINT",EDGE,{"derivedFrom":sQuery(id+"F0.wireOp",EDGE,"E22")}),1.0]])]});
            var Q6;
            Q6=makeQuery(id+"F0.imprint","IMPRINT",FACE,{"disambiguationData":[TD([[makeQuery(id+"F0.imprint","IMPRINT",EDGE,{"derivedFrom":sQuery(id+"F0.wireOp",EDGE,"E82.MirrorCS")}),-1.0]])]});
            var Q7;
            {var subQ3=sQuery(id+"F0.wireOp",EDGE,"E72.MirrorCS");Q7=makeQuery(id+"F0.imprint","IMPRINT",FACE,{"disambiguationData":[TD([[makeQuery(id+"F0.imprint","IMPRINT",EDGE,{"derivedFrom":subQ3}),-1.0]])]});}
            var Q8;
            Q8=makeQuery(id+"F0.imprint","IMPRINT",FACE,{"disambiguationData":[TD([[makeQuery(id+"F0.imprint","IMPRINT",EDGE,{"derivedFrom":sQuery(id+"F0.wireOp",EDGE,"E68.MirrorCS")}),-1.0]])]});
            var Q9;
            Q9=makeQuery(id+"F0.imprint","IMPRINT",FACE,{"disambiguationData":[TD([[makeQuery(id+"F0.imprint","IMPRINT",EDGE,{"derivedFrom":sQuery(id+"F0.wireOp",EDGE,"E39.MirrorCS")}),-1.0]])]});
            var Q10;
            {var subQ1=sQuery(id+"F0.wireOp",EDGE,"E35.MirrorCS");Q10=makeQuery(id+"F0.imprint","IMPRINT",FACE,{"disambiguationData":[TD([[makeQuery(id+"F0.imprint","IMPRINT",EDGE,{"derivedFrom":subQ1}),-1.0]])]});}
            var Q11;
            Q11=makeQuery(id+"F0.imprint","IMPRINT",FACE,{"disambiguationData":[TD([[makeQuery(id+"F0.imprint","IMPRINT",EDGE,{"derivedFrom":sQuery(id+"F0.wireOp",EDGE,"E34.MirrorCS")}),-1.0]])]});
            var Q12;
            Q12=makeQuery(id+"F0.imprint","IMPRINT",FACE,{"disambiguationData":[TD([[makeQuery(id+"F0.imprint","IMPRINT",EDGE,{"derivedFrom":sQuery(id+"F0.wireOp",EDGE,"E143")}),-1.0]])]});
            extrude(context, id + "F4", {"entities" : qUnion([Q0, Q1, Q2, Q3, Q4, Q5, Q6, Q7, Q8, Q9, Q10, Q11, Q12]), "operationType" : NewBodyOperationType.ADD, "depth" : 2 * mm, "offsetDistance" : 25 * mm});
        }
    });
